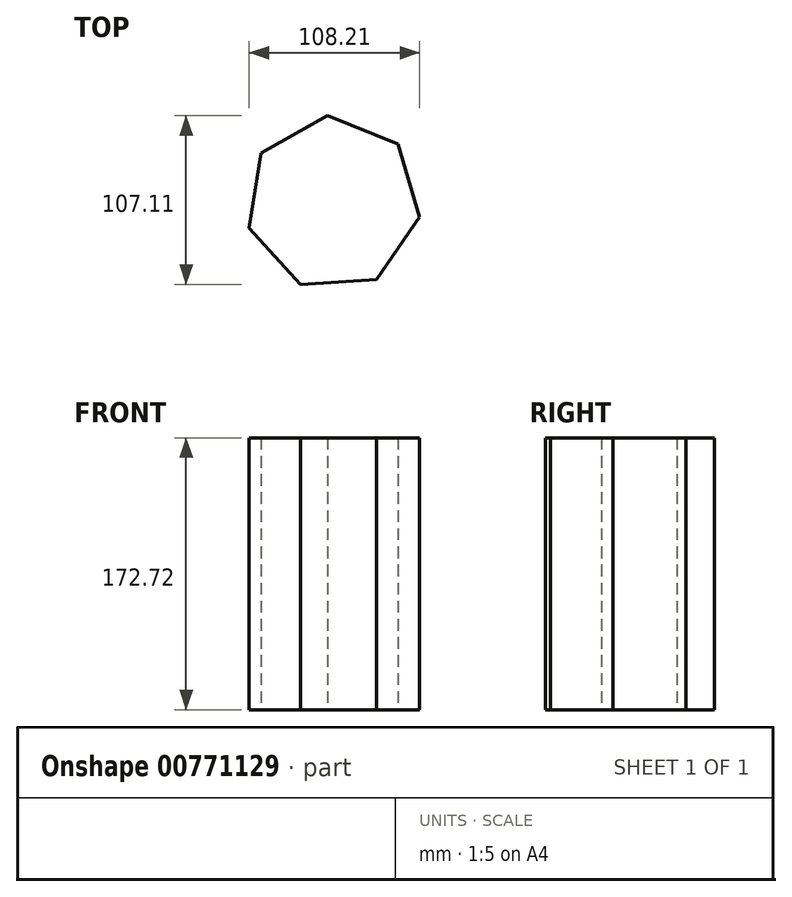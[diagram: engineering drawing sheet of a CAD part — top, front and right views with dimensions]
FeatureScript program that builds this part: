
annotation { "Feature Type Name" : "Feature", "Feature Type Description" : "" }
export const myFeature = defineFeature(function(context is Context, id is Id, definition is map)
    precondition{}
    {
        {
            var Q0;
            Q0=qCreatedBy(makeId("Top.planeOp"),FACE);
            var sketch = newSketch(context, id + "F0", { "sketchPlane" : qUnion([Q0])});
            skCircle(sketch, "E0.cCircle", {"center": v(0, 0) * mm, "radius": 50.11 * mm, "construction": true});
            skLineSegment(sketch, "E0.0", {"start": v(-20.74, -51.6) * mm, "end": v(-53.28, -15.96) * mm});
            skLineSegment(sketch, "E0.1", {"start": v(-53.28, -15.96) * mm, "end": v(-45.7, 31.7) * mm});
            skLineSegment(sketch, "E0.2", {"start": v(-45.7, 31.7) * mm, "end": v(-3.7, 55.5) * mm});
            skLineSegment(sketch, "E0.3", {"start": v(-3.7, 55.5) * mm, "end": v(41.08, 37.5) * mm});
            skLineSegment(sketch, "E0.4", {"start": v(41.08, 37.5) * mm, "end": v(54.93, -8.74) * mm});
            skLineSegment(sketch, "E0.5", {"start": v(54.93, -8.74) * mm, "end": v(27.42, -48.4) * mm});
            skLineSegment(sketch, "E0.6", {"start": v(27.42, -48.4) * mm, "end": v(-20.74, -51.6) * mm});
            skPoint(sketch, "E0.0.midPoint", {"position": v(-37.01, -33.78) * mm});
            skSolve(sketch);
        }
        {
            var Q0;
            Q0=makeQuery(id+"F0.imprint","IMPRINT",FACE,{"disambiguationData":[TD([[makeQuery(id+"F0.imprint","IMPRINT",EDGE,{"derivedFrom":sQuery(id+"F0.wireOp",EDGE,"E0.0")}),-1.0]])]});
            extrude(context, id + "F1", {"entities" : qUnion([Q0]), "endBound" : BoundingType.SYMMETRIC, "depth" : 172.72 * mm, "offsetDistance" : 25.4 * mm});
        }
    });
